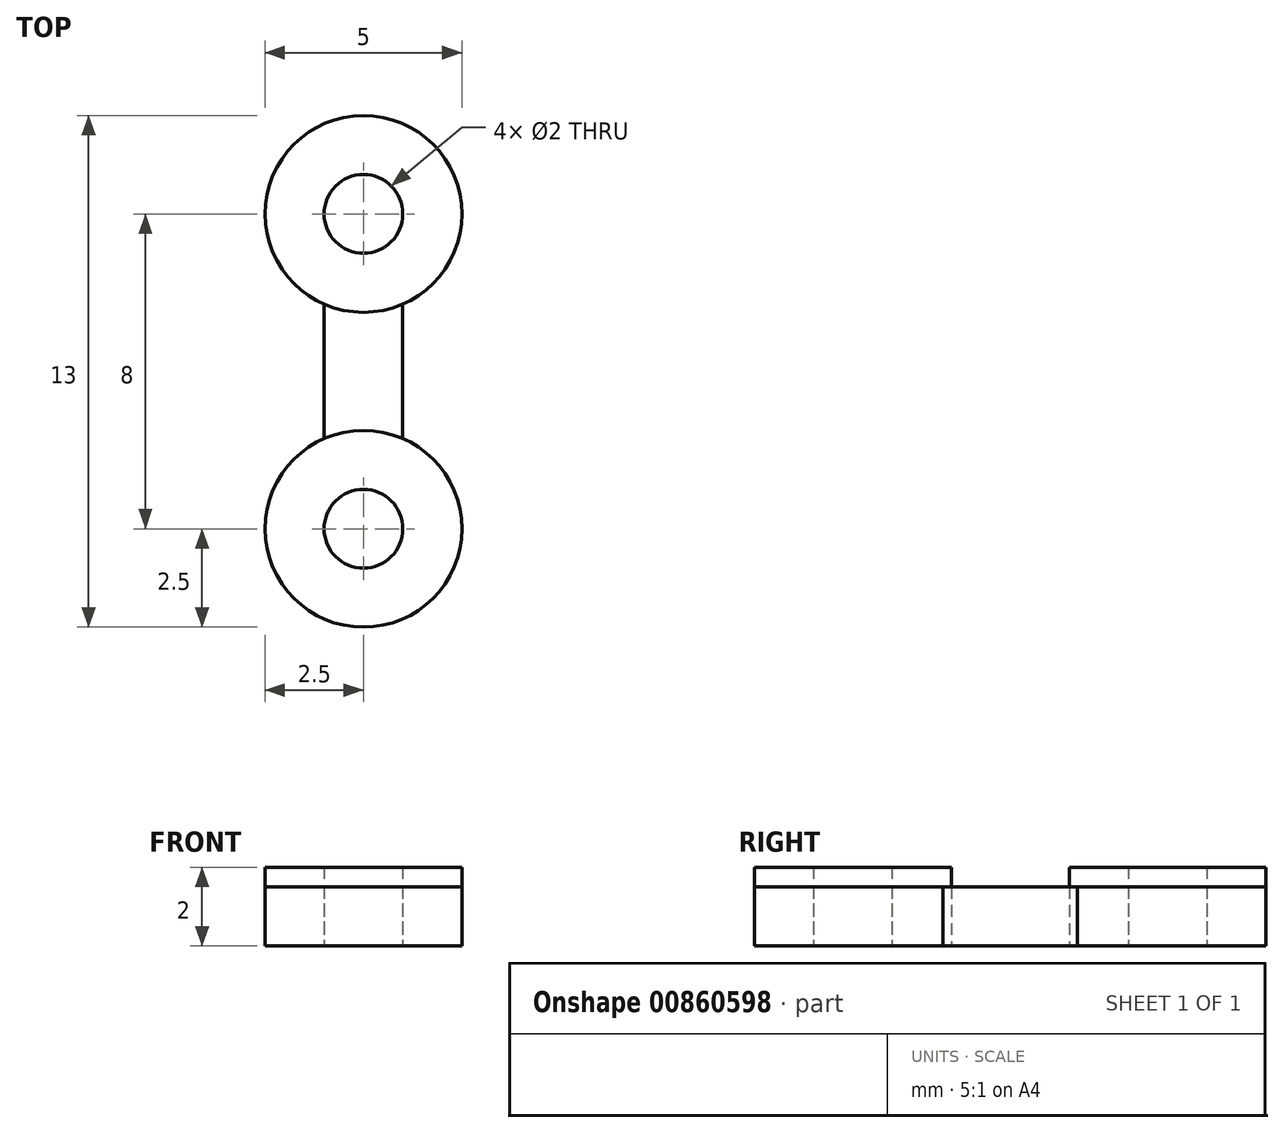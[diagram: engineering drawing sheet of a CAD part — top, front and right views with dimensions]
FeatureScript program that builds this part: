
annotation { "Feature Type Name" : "Feature", "Feature Type Description" : "" }
export const myFeature = defineFeature(function(context is Context, id is Id, definition is map)
    precondition{}
    {
        {
            var Q0;
            Q0=qCreatedBy(makeId("Top.planeOp"),FACE);
            var sketch = newSketch(context, id + "F0", { "sketchPlane" : qUnion([Q0])});
            skCircle(sketch, "E0", {"center": v(0, 0) * mm, "radius": 1 * mm});
            skCircle(sketch, "E1", {"center": v(0, 8) * mm, "radius": 1 * mm});
            skCircle(sketch, "E2", {"center": v(0, 0) * mm, "radius": 2.5 * mm});
            skCircle(sketch, "E3", {"center": v(0, 8) * mm, "radius": 2.5 * mm});
            skLineSegment(sketch, "E4", {"start": v(0, 8) * mm, "end": v(0, 0) * mm});
            skLineSegment(sketch, "E5.0", {"start": v(-1, 8) * mm, "end": v(-1, 0) * mm});
            skLineSegment(sketch, "E6.0", {"start": v(1, 8) * mm, "end": v(1, 0) * mm});
            skSolve(sketch);
        }
        {
            var Q0;
            {var subQ0=sQuery(id+"F0.wireOp",EDGE,"E5.0");var subQ1=sQuery(id+"F0.wireOp",EDGE,"E1");var subQ2=makeQuery(id+"F0.imprint","INTERSECT",VERTEX,{"derivedFrom":[subQ1,subQ0]});Q0=makeQuery(id+"F0.imprint","IMPRINT",FACE,{"disambiguationData":[TD([[makeQuery(id+"F0.imprint","IMPRINT",EDGE,{"disambiguationData":[TD([[subQ2,1.0]])],"derivedFrom":subQ1}),-1.0]])]});}
            var Q1;
            {var subQ0=sQuery(id+"F0.wireOp",EDGE,"E5.0");var subQ1=sQuery(id+"F0.wireOp",EDGE,"E1");var subQ2=makeQuery(id+"F0.imprint","INTERSECT",VERTEX,{"derivedFrom":[subQ1,subQ0]});Q1=makeQuery(id+"F0.imprint","IMPRINT",FACE,{"disambiguationData":[TD([[makeQuery(id+"F0.imprint","IMPRINT",EDGE,{"disambiguationData":[TD([[subQ2,-1.0]])],"derivedFrom":subQ1}),-1.0]])]});}
            var Q2;
            {var subQ0=sQuery(id+"F0.wireOp",EDGE,"E6.0");var subQ1=sQuery(id+"F0.wireOp",EDGE,"E1");var subQ2=makeQuery(id+"F0.imprint","INTERSECT",VERTEX,{"derivedFrom":[subQ1,subQ0]});Q2=makeQuery(id+"F0.imprint","IMPRINT",FACE,{"disambiguationData":[TD([[makeQuery(id+"F0.imprint","IMPRINT",EDGE,{"disambiguationData":[TD([[subQ2,1.0]])],"derivedFrom":subQ1}),-1.0]])]});}
            var Q3;
            {var subQ0=sQuery(id+"F0.wireOp",EDGE,"E5.0");var subQ1=sQuery(id+"F0.wireOp",EDGE,"E0");var subQ2=makeQuery(id+"F0.imprint","INTERSECT",VERTEX,{"derivedFrom":[subQ1,subQ0]});Q3=makeQuery(id+"F0.imprint","IMPRINT",FACE,{"disambiguationData":[TD([[makeQuery(id+"F0.imprint","IMPRINT",EDGE,{"disambiguationData":[TD([[subQ2,1.0]])],"derivedFrom":subQ1}),-1.0]])]});}
            var Q4;
            {var subQ0=sQuery(id+"F0.wireOp",EDGE,"E5.0");var subQ1=sQuery(id+"F0.wireOp",EDGE,"E0");var subQ2=makeQuery(id+"F0.imprint","INTERSECT",VERTEX,{"derivedFrom":[subQ1,subQ0]});Q4=makeQuery(id+"F0.imprint","IMPRINT",FACE,{"disambiguationData":[TD([[makeQuery(id+"F0.imprint","IMPRINT",EDGE,{"disambiguationData":[TD([[subQ2,-1.0]])],"derivedFrom":subQ1}),-1.0]])]});}
            var Q5;
            {var subQ0=sQuery(id+"F0.wireOp",EDGE,"E6.0");var subQ1=sQuery(id+"F0.wireOp",EDGE,"E0");var subQ2=makeQuery(id+"F0.imprint","INTERSECT",VERTEX,{"derivedFrom":[subQ1,subQ0]});Q5=makeQuery(id+"F0.imprint","IMPRINT",FACE,{"disambiguationData":[TD([[makeQuery(id+"F0.imprint","IMPRINT",EDGE,{"disambiguationData":[TD([[subQ2,-1.0]])],"derivedFrom":subQ1}),-1.0]])]});}
            extrude(context, id + "F1", {"entities" : qUnion([Q0, Q1, Q2, Q3, Q4, Q5]), "depth" : 2 * mm, "offsetDistance" : 25 * mm});
        }
        {
            var Q0;
            {var subQ0=sQuery(id+"F0.wireOp",EDGE,"E6.0");var subQ1=sQuery(id+"F0.wireOp",EDGE,"E2");var subQ2=makeQuery(id+"F0.imprint","INTERSECT",VERTEX,{"derivedFrom":[subQ1,subQ0]});Q0=makeQuery(id+"F0.imprint","IMPRINT",FACE,{"disambiguationData":[TD([[makeQuery(id+"F0.imprint","IMPRINT",EDGE,{"disambiguationData":[TD([[subQ2,-1.0]])],"derivedFrom":subQ1}),-1.0]])]});}
            var Q1;
            {var subQ0=sQuery(id+"F0.wireOp",EDGE,"E5.0");var subQ1=sQuery(id+"F0.wireOp",EDGE,"E2");var subQ2=makeQuery(id+"F0.imprint","INTERSECT",VERTEX,{"derivedFrom":[subQ1,subQ0]});Q1=makeQuery(id+"F0.imprint","IMPRINT",FACE,{"disambiguationData":[TD([[makeQuery(id+"F0.imprint","IMPRINT",EDGE,{"disambiguationData":[TD([[subQ2,1.0]])],"derivedFrom":subQ1}),-1.0]])]});}
            var Q2;
            Q2 = qSketchRegion(id + "F0", true);
            extrude(context, id + "F2", {"entities" : qUnion([Q0, Q1, Q2]), "depth" : 1.5 * mm, "offsetDistance" : 25 * mm});
        }
    });
